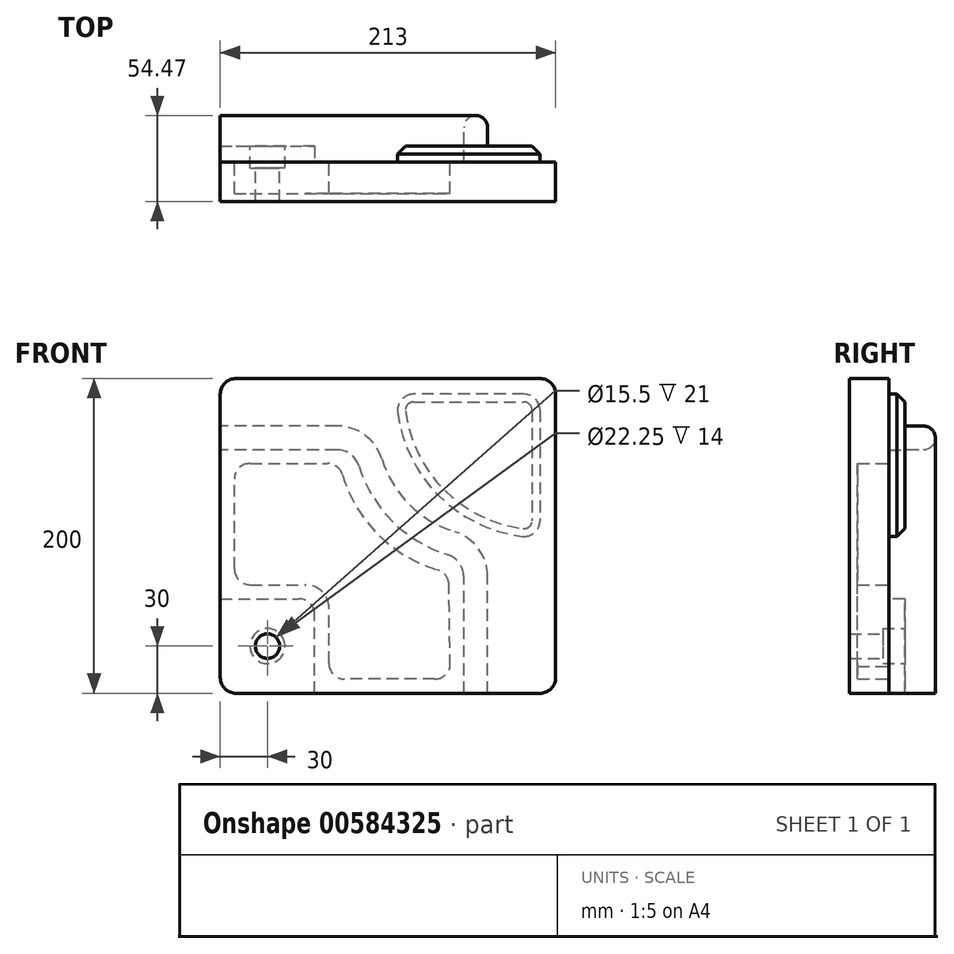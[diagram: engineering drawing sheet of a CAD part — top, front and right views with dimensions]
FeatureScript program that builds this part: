
annotation { "Feature Type Name" : "Feature", "Feature Type Description" : "" }
export const myFeature = defineFeature(function(context is Context, id is Id, definition is map)
    precondition{}
    {
        {
            var Q0;
            Q0=qCreatedBy(makeId("Front.planeOp"),FACE);
            var sketch = newSketch(context, id + "F0", { "sketchPlane" : qUnion([Q0])});
            skLineSegment(sketch, "E0.bottom", {"start": v(10, 200) * mm, "end": v(203, 200) * mm});
            skLineSegment(sketch, "E0.top", {"start": v(0, 0) * mm, "end": v(203, 0) * mm});
            skLineSegment(sketch, "E0.left", {"start": v(0, 190) * mm, "end": v(0, 0) * mm});
            skLineSegment(sketch, "E0.right", {"start": v(213, 190) * mm, "end": v(213, 10) * mm});
            skLineSegment(sketch, "E1", {"start": v(0, 0) * mm, "end": v(213, 0) * mm, "construction": true});
            skLineSegment(sketch, "E2", {"start": v(0, 200) * mm, "end": v(0, 0) * mm, "construction": true});
            skLineSegment(sketch, "E3.bottom", {"start": v(0, 0) * mm, "end": v(170, 0) * mm});
            skLineSegment(sketch, "E3.left", {"start": v(0, 0) * mm, "end": v(0, 170) * mm});
            skLineSegment(sketch, "E3.right", {"start": v(170, 0) * mm, "end": v(170, 77) * mm, "construction": true});
            skLineSegment(sketch, "E4.bottom", {"start": v(0, 0) * mm, "end": v(60, 0) * mm});
            skLineSegment(sketch, "E4.top", {"start": v(0, 60) * mm, "end": v(50, 60) * mm});
            skLineSegment(sketch, "E4.left", {"start": v(0, 0) * mm, "end": v(0, 60) * mm});
            skLineSegment(sketch, "E4.right", {"start": v(60, 0) * mm, "end": v(60, 50) * mm});
            skCircle(sketch, "E5", {"center": v(30, 30) * mm, "radius": 7.5 * mm});
            skLineSegment(sketch, "E6", {"start": v(30, 30) * mm, "end": v(0, 30) * mm, "construction": true});
            skLineSegment(sketch, "E7", {"start": v(30, 30) * mm, "end": v(30, 0) * mm, "construction": true});
            skLineSegment(sketch, "E8.bottom", {"start": v(0, 0) * mm, "end": v(69, 0) * mm});
            skLineSegment(sketch, "E8.top", {"start": v(19, 69) * mm, "end": v(54, 69) * mm});
            skLineSegment(sketch, "E8.left", {"start": v(0, 0) * mm, "end": v(0, 69) * mm});
            skLineSegment(sketch, "E8.right", {"start": v(69, 19) * mm, "end": v(69, 54) * mm});
            skLineSegment(sketch, "E9.bottom", {"start": v(0, 0) * mm, "end": v(155, 0) * mm});
            skLineSegment(sketch, "E9.top", {"start": v(0, 155) * mm, "end": v(74.08, 155) * mm});
            skLineSegment(sketch, "E9.left", {"start": v(0, 0) * mm, "end": v(0, 155) * mm});
            skLineSegment(sketch, "E10.bottom", {"start": v(0, 0) * mm, "end": v(141.4, 0) * mm});
            skLineSegment(sketch, "E10.top", {"start": v(19, 146) * mm, "end": v(68.02, 146) * mm});
            skLineSegment(sketch, "E10.left", {"start": v(0, 0) * mm, "end": v(0, 146) * mm});
            skPoint(sketch, "E11.visualSharp", {"position": v(60, 60) * mm});
            skArc(sketch, "E11.filletArc", {"start": v(60, 50) * mm, "mid": v(57.07, 57.07) * mm, "end": v(50, 60) * mm});
            skPoint(sketch, "E12.visualSharp", {"position": v(213, 200) * mm});
            skArc(sketch, "E12.filletArc", {"start": v(213, 190) * mm, "mid": v(210.07, 197.07) * mm, "end": v(203, 200) * mm});
            skLineSegment(sketch, "E13", {"start": v(69, 69) * mm, "end": v(69, 170) * mm, "construction": true});
            skLineSegment(sketch, "E14", {"start": v(69, 69) * mm, "end": v(155, 69) * mm, "construction": true});
            skArc(sketch, "E15", {"start": v(88.4, 144.48) * mm, "mid": v(109.54, 109.54) * mm, "end": v(144.48, 88.4) * mm});
            skPoint(sketch, "E16", {"position": v(170, 77) * mm});
            skPoint(sketch, "E17", {"position": v(170, 75) * mm});
            skPoint(sketch, "E18.visualSharp", {"position": v(69, 69) * mm});
            skArc(sketch, "E18.filletArc", {"start": v(69, 54) * mm, "mid": v(64.6, 64.6) * mm, "end": v(54, 69) * mm});
            skLineSegment(sketch, "E19", {"start": v(9, 79) * mm, "end": v(9, 136) * mm});
            skLineSegment(sketch, "E20", {"start": v(136.16, 9) * mm, "end": v(79, 9) * mm});
            skArc(sketch, "E21.filletArc", {"start": v(136.16, 9) * mm, "mid": v(142.57, 11.32) * mm, "end": v(146, 17.2) * mm});
            skPoint(sketch, "E22.visualSharp", {"position": v(9, 146) * mm});
            skArc(sketch, "E22.filletArc", {"start": v(19, 146) * mm, "mid": v(11.93, 143.07) * mm, "end": v(9, 136) * mm});
            skPoint(sketch, "E23.visualSharp", {"position": v(9, 69) * mm});
            skArc(sketch, "E23.filletArc", {"start": v(9, 79) * mm, "mid": v(11.93, 71.93) * mm, "end": v(19, 69) * mm});
            skPoint(sketch, "E24.visualSharp", {"position": v(69, 9) * mm});
            skArc(sketch, "E24.filletArc", {"start": v(69, 19) * mm, "mid": v(71.93, 11.93) * mm, "end": v(79, 9) * mm});
            skArc(sketch, "E25.trimOffspring", {"start": v(77.6, 138.84) * mm, "mid": v(100.14, 100.96) * mm, "end": v(138.02, 78.43) * mm});
            skPoint(sketch, "E26.visualSharp", {"position": v(145.06, 76.66) * mm});
            skArc(sketch, "E27.filletArc", {"start": v(77.6, 138.84) * mm, "mid": v(74, 144.01) * mm, "end": v(68.02, 146) * mm});
            skPoint(sketch, "E28", {"position": v(155, 85.83) * mm});
            skArc(sketch, "E29", {"start": v(101.96, 151.54) * mm, "mid": v(120.15, 120.15) * mm, "end": v(151.54, 101.96) * mm});
            skLineSegment(sketch, "E30", {"start": v(170, 0) * mm, "end": v(170, 77.83) * mm});
            skLineSegment(sketch, "E31", {"start": v(0, 170) * mm, "end": v(77.83, 170) * mm});
            skLineSegment(sketch, "E32.trimOffspring", {"start": v(155, 69) * mm, "end": v(155, 74.08) * mm});
            skArc(sketch, "E33.filletArc", {"start": v(155, 74.08) * mm, "mid": v(152.09, 82.97) * mm, "end": v(144.48, 88.4) * mm});
            skArc(sketch, "E34.filletArc", {"start": v(88.4, 144.48) * mm, "mid": v(82.97, 152.09) * mm, "end": v(74.08, 155) * mm});
            skLineSegment(sketch, "E35", {"start": v(146, 17.2) * mm, "end": v(145.19, 69) * mm});
            skLineSegment(sketch, "E36", {"start": v(155, 69) * mm, "end": v(155, 0) * mm});
            skArc(sketch, "E37.filletArc", {"start": v(145.19, 69) * mm, "mid": v(143.15, 74.89) * mm, "end": v(138.02, 78.43) * mm});
            skArc(sketch, "E38.filletArc", {"start": v(170, 77.83) * mm, "mid": v(164.86, 93.02) * mm, "end": v(151.54, 101.96) * mm});
            skArc(sketch, "E39.filletArc", {"start": v(101.96, 151.54) * mm, "mid": v(93.02, 164.86) * mm, "end": v(77.83, 170) * mm});
            skArc(sketch, "E40", {"start": v(112.7, 178.77) * mm, "mid": v(138.65, 125.65) * mm, "end": v(191.77, 99.7) * mm});
            skLineSegment(sketch, "E41", {"start": v(203, 190) * mm, "end": v(122.62, 190) * mm});
            skLineSegment(sketch, "E42", {"start": v(203, 190) * mm, "end": v(203, 109.62) * mm});
            skPoint(sketch, "E43.visualSharp", {"position": v(203, 99) * mm});
            skArc(sketch, "E43.filletArc", {"start": v(191.77, 99.7) * mm, "mid": v(199.62, 102.12) * mm, "end": v(203, 109.62) * mm});
            skPoint(sketch, "E44.visualSharp", {"position": v(112, 190) * mm});
            skArc(sketch, "E44.filletArc", {"start": v(122.62, 190) * mm, "mid": v(115.12, 186.62) * mm, "end": v(112.7, 178.77) * mm});
            skPoint(sketch, "E45.visualSharp", {"position": v(0, 200) * mm});
            skArc(sketch, "E45.filletArc", {"start": v(10, 200) * mm, "mid": v(2.93, 197.07) * mm, "end": v(0, 190) * mm});
            skPoint(sketch, "E46.visualSharp", {"position": v(213, 0) * mm});
            skArc(sketch, "E46.filletArc", {"start": v(203, 0) * mm, "mid": v(210.07, 2.93) * mm, "end": v(213, 10) * mm});
            skSolve(sketch);
        }
        {
            var Q0;
            Q0 = qSketchRegion(id + "F0", true);
            var Q1;
            Q1=makeQuery(id+"F0.imprint","IMPRINT",FACE,{"disambiguationData":[TD([[makeQuery(id+"F0.imprint","IMPRINT",EDGE,{"derivedFrom":sQuery(id+"F0.wireOp",EDGE,"E40")}),1.0]])]});
            var Q2;
            Q2=makeQuery(id+"F0.imprint","IMPRINT",FACE,{"disambiguationData":[TD([[makeQuery(id+"F0.imprint","IMPRINT",EDGE,{"derivedFrom":sQuery(id+"F0.wireOp",EDGE,"E8.top")}),1.0]])]});
            extrude(context, id + "F1", {"entities" : qUnion([Q0, Q1, Q2]), "depth" : 25 * mm, "offsetDistance" : 25 * mm});
        }
        {
            var Q0;
            Q0=makeQuery(id+"F0.imprint","IMPRINT",FACE,{"disambiguationData":[TD([[makeQuery(id+"F0.imprint","IMPRINT",EDGE,{"derivedFrom":sQuery(id+"F0.wireOp",EDGE,"E8.top")}),1.0]])]});
            var sketch = newSketch(context, id + "F2", { "sketchPlane" : qUnion([Q0])});
            skArc(sketch, "E47.0.0", {"start": v(138.02, 78.43) * mm, "mid": v(100.14, 100.96) * mm, "end": v(77.6, 138.84) * mm});
            skArc(sketch, "E47.0.1", {"start": v(77.6, 138.84) * mm, "mid": v(74, 144.01) * mm, "end": v(68.02, 146) * mm});
            skLineSegment(sketch, "E47.0.2", {"start": v(68.02, 146) * mm, "end": v(19, 146) * mm});
            skArc(sketch, "E47.0.3", {"start": v(19, 146) * mm, "mid": v(11.93, 143.07) * mm, "end": v(9, 136) * mm});
            skLineSegment(sketch, "E47.0.4", {"start": v(9, 136) * mm, "end": v(9, 79) * mm});
            skArc(sketch, "E47.0.5", {"start": v(9, 79) * mm, "mid": v(11.93, 71.93) * mm, "end": v(19, 69) * mm});
            skLineSegment(sketch, "E47.0.6", {"start": v(19, 69) * mm, "end": v(54, 69) * mm});
            skArc(sketch, "E47.0.7", {"start": v(54, 69) * mm, "mid": v(64.6, 64.6) * mm, "end": v(69, 54) * mm});
            skLineSegment(sketch, "E47.0.8", {"start": v(69, 54) * mm, "end": v(69, 19) * mm});
            skArc(sketch, "E47.0.9", {"start": v(69, 19) * mm, "mid": v(71.93, 11.93) * mm, "end": v(79, 9) * mm});
            skLineSegment(sketch, "E47.0.10", {"start": v(79, 9) * mm, "end": v(136.16, 9) * mm});
            skArc(sketch, "E47.0.11", {"start": v(136.16, 9) * mm, "mid": v(142.57, 11.32) * mm, "end": v(146, 17.2) * mm});
            skLineSegment(sketch, "E47.0.12", {"start": v(146, 17.2) * mm, "end": v(145.19, 69) * mm});
            skArc(sketch, "E47.0.13", {"start": v(145.19, 69) * mm, "mid": v(143.15, 74.89) * mm, "end": v(138.02, 78.43) * mm});
            skSolve(sketch);
        }
        {
            var Q0;
            Q0 = qSketchRegion(id + "F2", true);
            extrude(context, id + "F3", {"entities" : qUnion([Q0]), "operationType" : NewBodyOperationType.REMOVE, "depth" : 20 * mm, "offsetDistance" : 25 * mm});
        }
        {
            var Q0;
            {var subQ4=sQuery(id+"F0.wireOp",EDGE,"E4.top");Q0=makeQuery(id+"F0.imprint","IMPRINT",FACE,{"disambiguationData":[TD([[makeQuery(id+"F0.imprint","IMPRINT",EDGE,{"derivedFrom":subQ4}),-1.0]])]});}
            var sketch = newSketch(context, id + "F4", { "sketchPlane" : qUnion([Q0])});
            skCircle(sketch, "E48.0", {"center": v(30, 30) * mm, "radius": 7.5 * mm});
            skLineSegment(sketch, "E49.0.0", {"start": v(0, 0) * mm, "end": v(60, 0) * mm});
            skLineSegment(sketch, "E49.0.1", {"start": v(60, 0) * mm, "end": v(60, 50) * mm});
            skArc(sketch, "E49.0.2", {"start": v(60, 50) * mm, "mid": v(57.07, 57.07) * mm, "end": v(50, 60) * mm});
            skLineSegment(sketch, "E49.0.3", {"start": v(50, 60) * mm, "end": v(0, 60) * mm});
            skLineSegment(sketch, "E49.0.4", {"start": v(0, 60) * mm, "end": v(0, 0) * mm});
            skSolve(sketch);
        }
        {
            var Q0;
            Q0 = qSketchRegion(id + "F4", true);
            extrude(context, id + "F5", {"entities" : qUnion([Q0]), "operationType" : NewBodyOperationType.ADD, "oppositeDirection" : true, "depth" : 10 * mm, "offsetDistance" : 25 * mm});
        }
        {
            var Q0;
            Q0=makeQuery(id+"F5.opExtrude","CAP_FACE",FACE,{"disambiguationData":[OSD([sQuery(id+"F4.wireOp",EDGE,"E48.0"),sQuery(id+"F4.wireOp",EDGE,"E49.0.0"),sQuery(id+"F4.wireOp",EDGE,"E49.0.1"),sQuery(id+"F4.wireOp",EDGE,"E49.0.2"),sQuery(id+"F4.wireOp",EDGE,"E49.0.3"),sQuery(id+"F4.wireOp",EDGE,"E49.0.4")])],"isStart":false});
            var sketch = newSketch(context, id + "F6", { "sketchPlane" : qUnion([Q0])});
            skPoint(sketch, "E50.0", {"position": v(-30, 30) * mm});
            skSolve(sketch);
        }
        {
            var Q0;
            Q0=sQuery(id+"F6.wireOp",VERTEX,"E50.0");
            var Q1;
            Q1=makeQuery(id+"F1.opExtrude","SWEPT_BODY",BODY,{"disambiguationData":[OSD([sQuery(id+"F0.wireOp",EDGE,"E0.bottom"),sQuery(id+"F0.wireOp",EDGE,"E0.top"),sQuery(id+"F0.wireOp",EDGE,"E0.left"),sQuery(id+"F0.wireOp",EDGE,"E0.right"),sQuery(id+"F0.wireOp",EDGE,"E3.bottom"),sQuery(id+"F0.wireOp",EDGE,"E3.left"),sQuery(id+"F0.wireOp",EDGE,"E5"),sQuery(id+"F0.wireOp",EDGE,"E9.bottom"),sQuery(id+"F0.wireOp",EDGE,"E9.left"),sQuery(id+"F0.wireOp",EDGE,"E10.bottom"),sQuery(id+"F0.wireOp",EDGE,"E10.left"),sQuery(id+"F0.wireOp",EDGE,"E12.filletArc"),sQuery(id+"F0.wireOp",EDGE,"E45.filletArc"),sQuery(id+"F0.wireOp",EDGE,"E46.filletArc")])]});
            hole(context, id + "F7", {"style" : HoleStyle.C_BORE, "endStyle" : HoleEndStyle.THROUGH, "standardTappedOrClearance" : lookupTablePath({ "standard" : "ISO", "fit" : "Normal", "size" : "M14", "type" : "Clearance" }), "standardBlindInLast" : lookupTablePath({ "fit" : "Standard", "standard" : "ISO", "size" : "M14", "type" : "Clearance" }), "holeDiameter" : 15.5 * mm, "cBoreDiameter" : 22.25 * mm, "cBoreDepth" : 14 * mm, "majorDiameter" : 5 * mm, "isTappedThrough" : true, "tappedDepth" : 12 * mm, "tapClearance" : 3, "locations" : qUnion([Q0]), "scope" : qUnion([Q1])});
        }
        {
            var Q0;
            Q0=makeQuery(id+"F5.boolean.opBoolean","MERGE",FACE,{"derivedFrom":[makeQuery(id+"F1.opExtrude","SWEPT_FACE",FACE,{"disambiguationData":[OSD([sQuery(id+"F0.wireOp",EDGE,"E0.top"),sQuery(id+"F0.wireOp",EDGE,"E3.bottom"),sQuery(id+"F0.wireOp",EDGE,"E9.bottom"),sQuery(id+"F0.wireOp",EDGE,"E10.bottom")])]}),makeQuery(id+"F5.opExtrude","SWEPT_FACE",FACE,{"disambiguationData":[OSD([sQuery(id+"F4.wireOp",EDGE,"E49.0.0")])]})]});
            var sketch = newSketch(context, id + "F8", { "sketchPlane" : qUnion([Q0])});
            skLineSegment(sketch, "E51", {"start": v(169.86, 0) * mm, "end": v(154.66, 0) * mm});
            skPoint(sketch, "E52.centerSnap0", {"position": v(162.26, 0) * mm});
            skArc(sketch, "E53", {"start": v(154.76, -22) * mm, "mid": v(162.26, -29.47) * mm, "end": v(169.76, -22) * mm});
            skLineSegment(sketch, "E54", {"start": v(169.86, 0) * mm, "end": v(169.76, -22) * mm});
            skLineSegment(sketch, "E55", {"start": v(154.66, 0) * mm, "end": v(154.76, -22) * mm});
            skSolve(sketch);
        }
        {
            var Q0;
            Q0=makeQuery(id+"F8.imprint","IMPRINT",FACE,{"disambiguationData":[TD([[makeQuery(id+"F8.imprint","IMPRINT",EDGE,{"derivedFrom":sQuery(id+"F8.wireOp",EDGE,"E51")}),-1.0]])]});
            var Q1;
            Q1=sQuery(id+"F0.wireOp",EDGE,"E36");
            var Q2;
            Q2=sQuery(id+"F0.wireOp",EDGE,"E33.filletArc");
            var Q3;
            Q3=sQuery(id+"F0.wireOp",EDGE,"E15");
            var Q4;
            Q4=sQuery(id+"F0.wireOp",EDGE,"E32.trimOffspring");
            var Q5;
            Q5=sQuery(id+"F0.wireOp",EDGE,"E34.filletArc");
            var Q6;
            Q6=sQuery(id+"F0.wireOp",EDGE,"E9.top");
            sweep(context, id + "F9", {"operationType" : NewBodyOperationType.ADD, "profiles" : qUnion([Q0]), "path" : qUnion([Q1, Q2, Q3, Q4, Q5, Q6])});
        }
        {
            var Q0;
            Q0=makeQuery(id+"F0.imprint","IMPRINT",FACE,{"disambiguationData":[TD([[makeQuery(id+"F0.imprint","IMPRINT",EDGE,{"derivedFrom":sQuery(id+"F0.wireOp",EDGE,"E40")}),1.0]])]});
            extrude(context, id + "F10", {"entities" : qUnion([Q0]), "operationType" : NewBodyOperationType.ADD, "oppositeDirection" : true, "depth" : 10 * mm, "offsetDistance" : 25 * mm});
        }
        {
            var Q0;
            Q0=makeQuery(id+"F10.opExtrude","SWEPT_EDGE",EDGE,{"disambiguationData":[OSD([sQuery(id+"F0.wireOp",EDGE,"E41"),sQuery(id+"F0.wireOp",EDGE,"E42")])]});
            fillet(context, id + "F11", {"entities" : qUnion([Q0]), "radius" : 10 * mm, "tangentPropagation" : true, "allowEdgeOverflow" : false});
        }
        {
            var Q0;
            Q0=makeQuery(id+"F5.boolean.opBoolean","MERGE",EDGE,{"derivedFrom":[makeQuery(id+"F1.opExtrude","SWEPT_EDGE",EDGE,{"disambiguationData":[OSD([sQuery(id+"F0.wireOp",EDGE,"E10.bottom"),sQuery(id+"F0.wireOp",EDGE,"E10.left")])]}),makeQuery(id+"F5.opExtrude","SWEPT_EDGE",EDGE,{"disambiguationData":[OSD([sQuery(id+"F4.wireOp",EDGE,"E49.0.0"),sQuery(id+"F4.wireOp",EDGE,"E49.0.4")])]})]});
            fillet(context, id + "F12", {"entities" : qUnion([Q0]), "radius" : 10 * mm, "tangentPropagation" : true, "allowEdgeOverflow" : false});
        }
        {
            var Q0;
            Q0=makeQuery(id+"F10.opExtrude","CAP_FACE",FACE,{"disambiguationData":[OSD([sQuery(id+"F0.wireOp",EDGE,"E40"),sQuery(id+"F0.wireOp",EDGE,"E41"),sQuery(id+"F0.wireOp",EDGE,"E42"),sQuery(id+"F0.wireOp",EDGE,"E43.filletArc"),sQuery(id+"F0.wireOp",EDGE,"E44.filletArc")])],"isStart":false});
            chamfer(context, id + "F13", {"entities" : qUnion([Q0]), "width" : 5 * mm, "tangentPropagation" : true});
        }
    });
